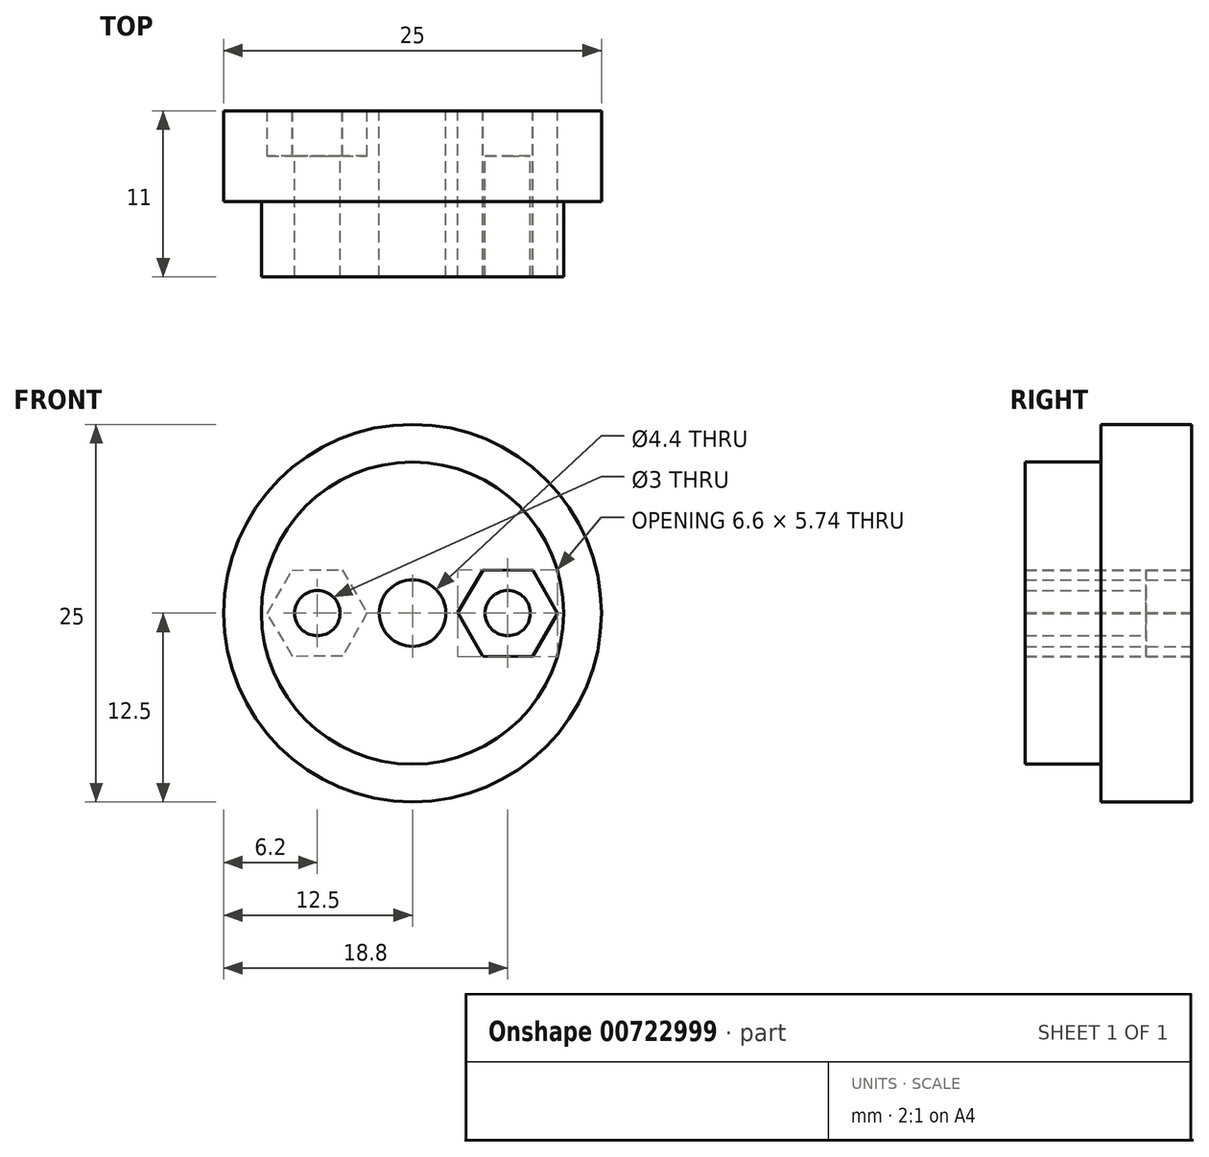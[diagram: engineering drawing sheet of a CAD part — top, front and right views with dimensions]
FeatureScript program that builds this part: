
annotation { "Feature Type Name" : "Feature", "Feature Type Description" : "" }
export const myFeature = defineFeature(function(context is Context, id is Id, definition is map)
    precondition{}
    {
        {
            var Q0;
            Q0=qCreatedBy(makeId("Front.planeOp"),FACE);
            var sketch = newSketch(context, id + "F0", { "sketchPlane" : qUnion([Q0])});
            skCircle(sketch, "E0", {"center": v(0, 0) * mm, "radius": 2.2 * mm});
            skCircle(sketch, "E1", {"center": v(0, 0) * mm, "radius": 10 * mm});
            skCircle(sketch, "E2", {"center": v(0, 0) * mm, "radius": 12.5 * mm});
            skSolve(sketch);
        }
        {
            var Q0;
            Q0=makeQuery(id+"F0.imprint","IMPRINT",FACE,{"disambiguationData":[TD([[makeQuery(id+"F0.imprint","IMPRINT",EDGE,{"derivedFrom":sQuery(id+"F0.wireOp",EDGE,"E1")}),-1.0]])]});
            extrude(context, id + "F1", {"entities" : qUnion([Q0]), "depth" : 6 * mm, "offsetDistance" : 25 * mm});
        }
        {
            var Q0;
            Q0=makeQuery(id+"F0.imprint","IMPRINT",FACE,{"disambiguationData":[TD([[makeQuery(id+"F0.imprint","IMPRINT",EDGE,{"derivedFrom":sQuery(id+"F0.wireOp",EDGE,"E0")}),-1.0]])]});
            extrude(context, id + "F2", {"entities" : qUnion([Q0]), "operationType" : NewBodyOperationType.ADD, "depth" : 11 * mm, "offsetDistance" : 25 * mm});
        }
        {
            var Q0;
            Q0=qCreatedBy(makeId("Front.planeOp"),FACE);
            var sketch = newSketch(context, id + "F3", { "sketchPlane" : qUnion([Q0])});
            skCircle(sketch, "E3", {"center": v(-6.3, 0) * mm, "radius": 1.5 * mm});
            skLineSegment(sketch, "E4.0", {"start": v(-7.93, -2.87) * mm, "end": v(-9.6, -0.02) * mm});
            skLineSegment(sketch, "E4.1", {"start": v(-9.6, -0.02) * mm, "end": v(-7.97, 2.85) * mm});
            skLineSegment(sketch, "E4.2", {"start": v(-7.97, 2.85) * mm, "end": v(-4.67, 2.87) * mm});
            skLineSegment(sketch, "E4.3", {"start": v(-4.67, 2.87) * mm, "end": v(-3, 0.02) * mm});
            skLineSegment(sketch, "E4.4", {"start": v(-3, 0.02) * mm, "end": v(-4.63, -2.85) * mm});
            skLineSegment(sketch, "E4.5", {"start": v(-4.63, -2.85) * mm, "end": v(-7.93, -2.87) * mm});
            skPoint(sketch, "E4.0.midPoint", {"position": v(-8.76, -1.45) * mm});
            skCircle(sketch, "E5.MirrorC", {"center": v(6.3, 0) * mm, "radius": 1.5 * mm});
            skLineSegment(sketch, "E6.MirrorCS", {"start": v(4.67, 2.87) * mm, "end": v(3, 0.02) * mm});
            skLineSegment(sketch, "E7.MirrorCS", {"start": v(3, 0.02) * mm, "end": v(4.63, -2.85) * mm});
            skLineSegment(sketch, "E8.MirrorCS", {"start": v(4.63, -2.85) * mm, "end": v(7.93, -2.87) * mm});
            skLineSegment(sketch, "E9.MirrorCS", {"start": v(7.93, -2.87) * mm, "end": v(9.6, -0.02) * mm});
            skLineSegment(sketch, "E10.MirrorCS", {"start": v(9.6, -0.02) * mm, "end": v(7.97, 2.85) * mm});
            skLineSegment(sketch, "E11.MirrorCS", {"start": v(7.97, 2.85) * mm, "end": v(4.67, 2.87) * mm});
            skSolve(sketch);
        }
        {
            var Q0;
            Q0=makeQuery(id+"F3.imprint","IMPRINT",FACE,{"disambiguationData":[TD([[makeQuery(id+"F3.imprint","IMPRINT",EDGE,{"derivedFrom":sQuery(id+"F3.wireOp",EDGE,"E5.MirrorC")}),-1.0]])]});
            var Q1;
            Q1=makeQuery(id+"F3.imprint","IMPRINT",FACE,{"disambiguationData":[TD([[makeQuery(id+"F3.imprint","IMPRINT",EDGE,{"derivedFrom":sQuery(id+"F3.wireOp",EDGE,"E3")}),1.0]])]});
            extrude(context, id + "F4", {"entities" : qUnion([Q0, Q1]), "operationType" : NewBodyOperationType.REMOVE, "depth" : 11 * mm, "offsetDistance" : 25 * mm});
        }
        {
            var Q0;
            Q0=makeQuery(id+"F3.imprint","IMPRINT",FACE,{"disambiguationData":[TD([[makeQuery(id+"F3.imprint","IMPRINT",EDGE,{"derivedFrom":sQuery(id+"F3.wireOp",EDGE,"E5.MirrorC")}),1.0]])]});
            var Q1;
            Q1=makeQuery(id+"F3.imprint","IMPRINT",FACE,{"disambiguationData":[TD([[makeQuery(id+"F3.imprint","IMPRINT",EDGE,{"derivedFrom":sQuery(id+"F3.wireOp",EDGE,"E3")}),-1.0]])]});
            extrude(context, id + "F5", {"entities" : qUnion([Q0, Q1]), "operationType" : NewBodyOperationType.REMOVE, "depth" : 3 * mm, "offsetDistance" : 25 * mm});
        }
    });
